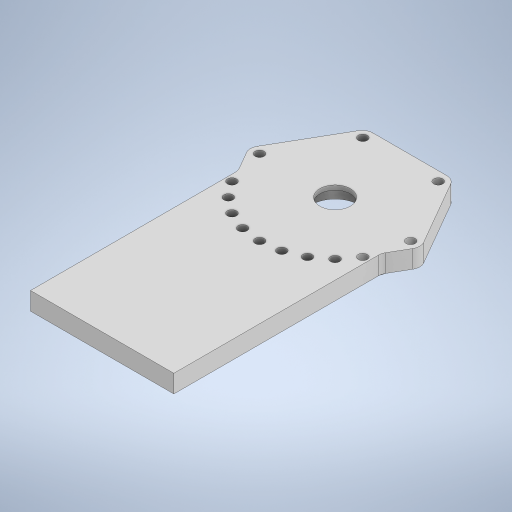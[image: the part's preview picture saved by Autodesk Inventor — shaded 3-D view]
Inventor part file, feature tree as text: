
AUTODESK INVENTOR PART (.ipt)
format: ipt  version: 2024 (Build 280153000, 153)  size: 371,712 bytes
history: native  units: mm
features: extrude x7, sketch x7, fillet x1, projected_geometry x1
ambient origin geometry x8: Origin, YZ Plane, XZ Plane, XY Plane, X Axis, Y Axis, Z Axis, Center Point
bodies: Solid1 (feature_tree)
feature tree (16):
  extrude  "Extrusion1"  Depth=10.0mm
  extrude  "Extrusion2"  Depth=20.0mm TaperAngle=0.0deg
  sketch  "Sketch3"  dims[d8=34.0mm d9=5.0mm d10=0.0mm]
  sketch  "Sketch4"  dims[d12=60.0mm d13=360.0deg d14=22.0mm d15=0.0mm]
  extrude  "Extrusion3"  Depth=5.0mm TaperAngle=0.0deg
  extrude  "Extrusion4"  Depth=22.0mm TaperAngle=0.0deg
  extrude  "Extrusion5"  Depth=20.0mm TaperAngle=0.0deg
  fillet  "Fillet1"  Radius=150.0mm
  extrude  "Extrusion6"  Depth=12.0mm
  extrude  "Extrusion7"  Depth=20.0mm
  sketch  "Sketch1"  dims[d0=250.0mm d1=160.0mm d2=160.0mm d3=10.0mm d4=52.0mm]
  sketch  "Sketch2"  dims[d5=80.0mm d6=20.0mm d7=0.0mm]
  sketch  "Sketch5"  dims[d17=60.0mm d18=360.0deg d19=20.0mm d20=0.0mm d21=150.0mm]
  sketch  "Sketch6"  dims[d22=5.0mm d23=0.0mm d24=12.0mm]
  projected_geometry  "Projected Loop1"
  sketch  "Sketch7"  dims[d25=20.0mm d26=20.0mm d27=12.0mm d28=0.0mm d29=84.286mm d30=10.0mm d31=240.0mm d33=360.0deg d35=39.0mm d36=0.0mm]
